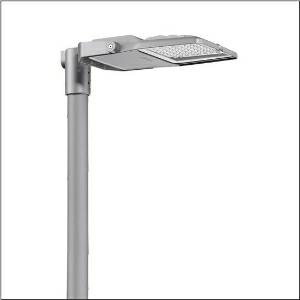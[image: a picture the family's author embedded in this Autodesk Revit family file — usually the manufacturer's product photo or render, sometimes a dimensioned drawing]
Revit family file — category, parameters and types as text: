
# Revit family: floodlight_fl_21_mini___pl33t_5xa7771b2f3a_0ade
name_source: partatom
category: Lighting Fixtures
units: mm (PartAtom-declared; Revit-internal decimal feet)

## family parameters
Cut with Voids When Loaded = No
Host = Face
Light Source = No
Part Type = Normal
Room Calculation Point = No
Round Connector Dimension = Use Diameter
Shared = No

## types (1)
- --- (1 x LED, 6170 lm, 45.5 W, 3000K)
    Apparent Load = 46 VA
    CIE Flux Codes = 26 75 99 100 100
    Color Rendering = 70
    Color Temperature = 3000K
    Default Elevation = 1800 mm
    Description = Floodlight FL 21 mini, floodlight, primary light control with lens, of PMMA, primary optical cover: protective disc, of toughened safety glass, transparent, light distribution: PL33T, light emission: direct distribution, installation type: surface-mounted, LED, High Power LED, rated luminous flux: 6.170lm, luminous efficacy: 136lm/W, light colour: 730, colour temperature: 3000K, control gear: ECG iQ, control: Auto-Match, Temp-Guard, Lumen-Switch, Night-Set, Smart-Wire, Light-Fading, Desk-Remote (wireless, voltage-free reading and setting of iQ features in the workshop via application-optimized NFC function/RFID function), optimised constant luminous flux control (CLO 2.0), with terminal, 6-pole, mains connection: 220..240V, AC, 50/60Hz, start of lifetime: 46W, end of lifetime: 48W, reduction: 22W, luminaire housing, of diecast aluminium, powder-coated, Siteco® metallic grey (DB 702S), corrosivity category C5 according to DIN EN ISO 12944, mast bracket, of steel, galvanised, powder-coated, Siteco® metallic grey (DB 702S), protection rating (complete): IP66, insulation class (complete): insulation class II (safety insulation), certification: CE, ENEC, VDE, protection symbol: D, impact resistance: IK08, permissible operating ambient temperature: -40..+40°C, permissible operating ambient temperature for outdoor applications: -40..+50°C, standard: DIN EN 12944, packaging unit: 1 piece

Light Distribution: PL33T
    Height = 70 mm
    Lamp = 1 x LED
    Lamp Light Flux = 6170 lm
    Lamp Power = 45.5 W
    Lamp count = 1
    Length = 485 mm
    Luminous efficacy = 136 lm/W
    Manufacturer = Siteco
    ModVariant = No
    Model = 5XA7771B2F3A
    Number of Poles = 1
    OnlyDefault = Yes
    Power Factor = 1
    Product Name = Floodlight FL 21 mini | PL33T
    Product group = floodlight | pylon top
    ProductGroupID = 6101
    Protection Class = Protection class II
    Protection Degree = IP 66
    RLX_Detail_Level = 1
    RlxData = <blob elided: 100977 chars, md5=bc80cbca>
    Socket = socket
    Standby Power = 0 W
    System Light Flux = 6170 lm
    System Power = 46 W
    Type Comments = factory setting: luminous flux: 100 % | dim-lin: 254 | 463 mA
    Type Image = l_1007125.jpg
    URL = http://relux.com
    VarID = @adj_060305
    Voltage = 0 V
    Weight = 0.00 kg
    Width = 337 mm

## geometry (parser evidence)
native form markers: Blend x4, Sweep x13
no freeform markers — native parametric forms only
